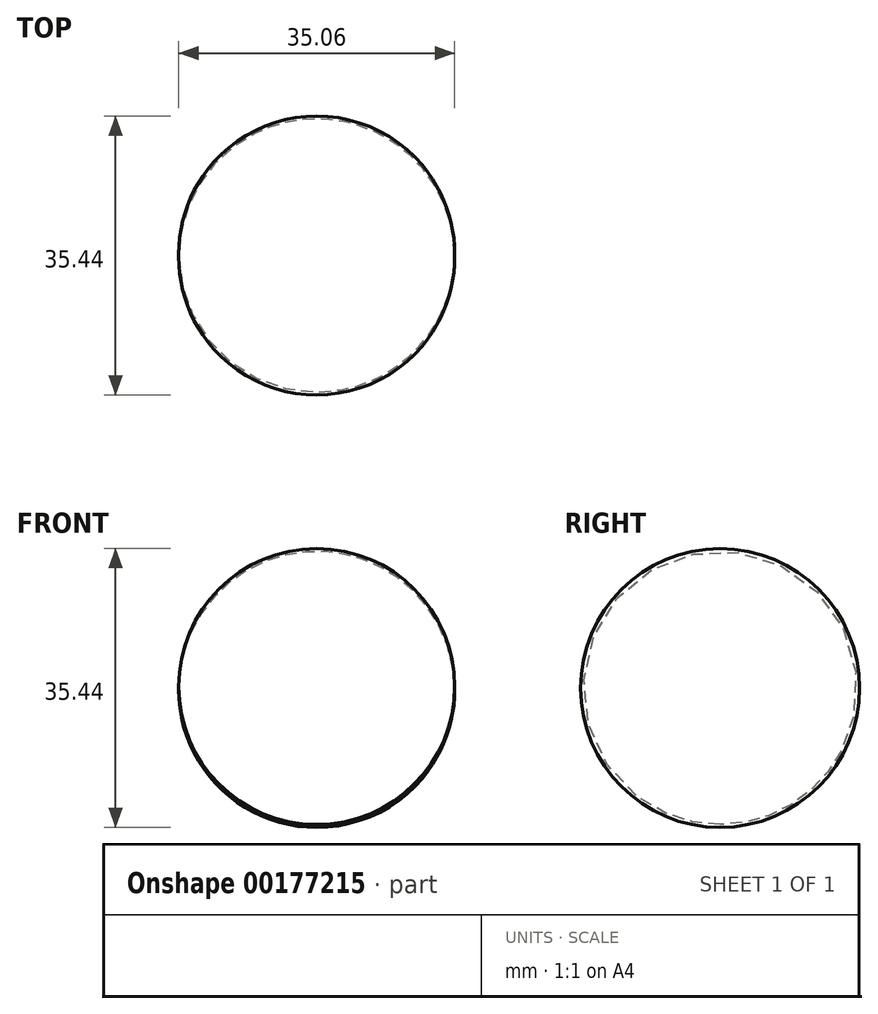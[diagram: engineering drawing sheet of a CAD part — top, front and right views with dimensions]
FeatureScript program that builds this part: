
annotation { "Feature Type Name" : "Feature", "Feature Type Description" : "" }
export const myFeature = defineFeature(function(context is Context, id is Id, definition is map)
    precondition{}
    {
        {
            var Q0;
            Q0=qCreatedBy(makeId("Top.planeOp"),FACE);
            var sketch = newSketch(context, id + "F0", { "sketchPlane" : qUnion([Q0])});
            skArc(sketch, "E0", {"start": v(35.06, 0) * mm, "mid": v(17.53, 17.35) * mm, "end": v(0, 0) * mm});
            skLineSegment(sketch, "E1", {"start": v(0, 0) * mm, "end": v(35.06, 0) * mm});
            skSolve(sketch);
        }
        {
            var Q0;
            Q0=makeQuery(id+"F0.imprint","IMPRINT",FACE,{"disambiguationData":[TD([[makeQuery(id+"F0.imprint","IMPRINT",EDGE,{"derivedFrom":sQuery(id+"F0.wireOp",EDGE,"E0")}),1.0]])]});
            var Q1;
            Q1=sQuery(id+"F0.wireOp",EDGE,"E1");
            revolve(context, id + "F1", {"entities" : qUnion([Q0]), "axis" : qUnion([Q1]), "revolveType" : RevolveType.FULL});
        }
    });
